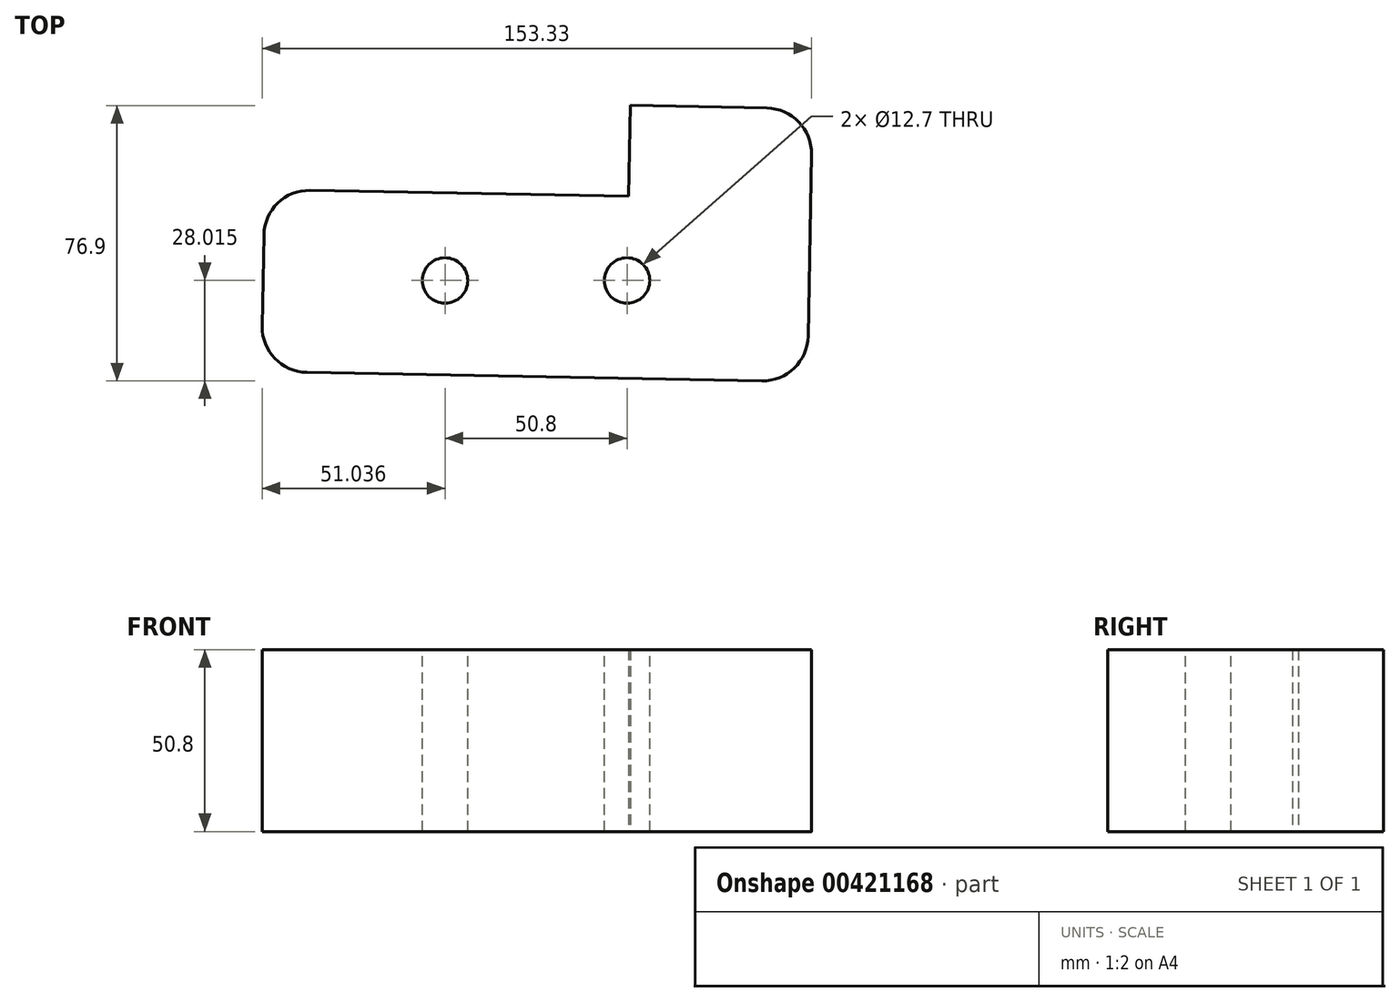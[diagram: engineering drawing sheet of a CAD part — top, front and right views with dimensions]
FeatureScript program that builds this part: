
annotation { "Feature Type Name" : "Feature", "Feature Type Description" : "" }
export const myFeature = defineFeature(function(context is Context, id is Id, definition is map)
    precondition{}
    {
        {
            var Q0;
            Q0=qCreatedBy(makeId("Top.planeOp"),FACE);
            var sketch = newSketch(context, id + "F0", { "sketchPlane" : qUnion([Q0])});
            skLineSegment(sketch, "E0", {"start": v(0, 0) * mm, "end": v(152.37, -2.86) * mm});
            skLineSegment(sketch, "E1", {"start": v(0, 0) * mm, "end": v(0.95, 50.8) * mm});
            skLineSegment(sketch, "E2", {"start": v(0.95, 50.8) * mm, "end": v(102.53, 48.89) * mm});
            skLineSegment(sketch, "E3", {"start": v(102.53, 48.89) * mm, "end": v(103.01, 74.28) * mm});
            skLineSegment(sketch, "E4", {"start": v(152.37, -2.86) * mm, "end": v(153.8, 73.33) * mm});
            skLineSegment(sketch, "E5", {"start": v(103.01, 74.28) * mm, "end": v(153.8, 73.33) * mm});
            skSolve(sketch);
        }
        {
            var Q0;
            Q0 = qSketchRegion(id + "F0", true);
            extrude(context, id + "F1", {"entities" : qUnion([Q0]), "depth" : 50.8 * mm});
        }
        {
            var Q0;
            Q0=makeQuery(id+"F1.opExtrude","SWEPT_EDGE",EDGE,{"disambiguationData":[OSD([sQuery(id+"F0.wireOp",EDGE,"E1"),sQuery(id+"F0.wireOp",EDGE,"E2")])]});
            var Q1;
            Q1=makeQuery(id+"F1.opExtrude","SWEPT_EDGE",EDGE,{"disambiguationData":[OSD([sQuery(id+"F0.wireOp",EDGE,"E0"),sQuery(id+"F0.wireOp",EDGE,"E1")])]});
            var Q2;
            Q2=makeQuery(id+"F1.opExtrude","SWEPT_EDGE",EDGE,{"disambiguationData":[OSD([sQuery(id+"F0.wireOp",EDGE,"E0"),sQuery(id+"F0.wireOp",EDGE,"E4")])]});
            var Q3;
            Q3=makeQuery(id+"F1.opExtrude","SWEPT_EDGE",EDGE,{"disambiguationData":[OSD([sQuery(id+"F0.wireOp",EDGE,"E4"),sQuery(id+"F0.wireOp",EDGE,"E5")])]});
            fillet(context, id + "F2", {"entities" : qUnion([Q0, Q1, Q2, Q3]), "radius" : 12.7 * mm, "tangentPropagation" : true, "allowEdgeOverflow" : false});
        }
        {
            var Q0;
            Q0=makeQuery(id+"F1.opExtrude","CAP_FACE",FACE,{"disambiguationData":[OSD([sQuery(id+"F0.wireOp",EDGE,"E0"),sQuery(id+"F0.wireOp",EDGE,"E1"),sQuery(id+"F0.wireOp",EDGE,"E2"),sQuery(id+"F0.wireOp",EDGE,"E3"),sQuery(id+"F0.wireOp",EDGE,"E4"),sQuery(id+"F0.wireOp",EDGE,"E5")])],"isStart":false});
            var sketch = newSketch(context, id + "F3", { "sketchPlane" : qUnion([Q0])});
            skPoint(sketch, "E6", {"position": v(51.28, 25.4) * mm});
            skPoint(sketch, "E7", {"position": v(102.08, 25.4) * mm});
            skSolve(sketch);
        }
        {
            var Q0;
            Q0=sQuery(id+"F3.wireOp",VERTEX,"E6");
            var Q1;
            Q1=sQuery(id+"F3.wireOp",VERTEX,"E7");
            var Q2;
            Q2=makeQuery(id+"F1.opExtrude","SWEPT_BODY",BODY,{"disambiguationData":[OSD([sQuery(id+"F0.wireOp",EDGE,"E0"),sQuery(id+"F0.wireOp",EDGE,"E1"),sQuery(id+"F0.wireOp",EDGE,"E2"),sQuery(id+"F0.wireOp",EDGE,"E3"),sQuery(id+"F0.wireOp",EDGE,"E4"),sQuery(id+"F0.wireOp",EDGE,"E5")])]});
            hole(context, id + "F4", {"style" : HoleStyle.SIMPLE, "endStyle" : HoleEndStyle.THROUGH, "holeDiameter" : 12.7 * mm, "isTappedThrough" : true, "tappedDepth" : 12.7 * mm, "tapClearance" : 3, "locations" : qUnion([Q0, Q1]), "scope" : qUnion([Q2])});
        }
    });
